annotation { "Feature Type Name" : "Feature", "Feature Type Description" : "" }
export const myFeature = defineFeature(function(context is Context, id is Id, definition is map)
    precondition{}
    {
        {
            var Q0;
            Q0=qCreatedBy(makeId("Top.planeOp"),FACE);
            var sketch = newSketch(context, id + "F0", { "sketchPlane" : qUnion([Q0])});
            skLineSegment(sketch, "E0.bottom", {"start": v(87.5, -50) * mm, "end": v(-62.5, -50) * mm});
            skLineSegment(sketch, "E0.top", {"start": v(87.5, 50) * mm, "end": v(-62.5, 50) * mm});
            skLineSegment(sketch, "E0.left", {"start": v(87.5, -50) * mm, "end": v(87.5, 50) * mm});
            skLineSegment(sketch, "E0.right", {"start": v(-87.5, -20) * mm, "end": v(-87.5, 20) * mm});
            skPoint(sketch, "E0.middle", {"position": v(0, 0) * mm});
            skPoint(sketch, "E1", {"position": v(-87.5, 20) * mm});
            skPoint(sketch, "E2", {"position": v(-62.5, 50) * mm});
            skArc(sketch, "E3", {"start": v(-87.5, 20) * mm, "mid": v(-72.08, 32.56) * mm, "end": v(-62.5, 50) * mm});
            skLineSegment(sketch, "E4", {"start": v(-87.5, 0) * mm, "end": v(87.5, 0) * mm, "construction": true});
            skArc(sketch, "E5.MirrorCS", {"start": v(-87.5, -20) * mm, "mid": v(-72.08, -32.56) * mm, "end": v(-62.5, -50) * mm});
            skPoint(sketch, "E6.orphan", {"position": v(-87.5, 50) * mm});
            skPoint(sketch, "E7.orphan", {"position": v(-87.5, -50) * mm});
            skSolve(sketch);
        }
        {
            var Q0;
            Q0 = qSketchRegion(id + "F0", true);
            extrude(context, id + "F1", {"entities" : qUnion([Q0]), "depth" : 3 * mm, "offsetDistance" : 25 * mm});
        }
        {
            var Q0;
            Q0=makeQuery(id+"F1.opExtrude","CAP_FACE",FACE,{"disambiguationData":[OSD([sQuery(id+"F0.wireOp",EDGE,"E0.bottom"),sQuery(id+"F0.wireOp",EDGE,"E0.top"),sQuery(id+"F0.wireOp",EDGE,"E0.left"),sQuery(id+"F0.wireOp",EDGE,"E0.right"),sQuery(id+"F0.wireOp",EDGE,"E3"),sQuery(id+"F0.wireOp",EDGE,"E5.MirrorCS")])],"isStart":false});
            var sketch = newSketch(context, id + "F2", { "sketchPlane" : qUnion([Q0])});
            skLineSegment(sketch, "E8", {"start": v(-62.5, 50) * mm, "end": v(-62.5, -50) * mm, "construction": true});
            skLineSegment(sketch, "E9", {"start": v(-62.5, 0) * mm, "end": v(-75, 0) * mm, "construction": true});
            skPoint(sketch, "E10", {"position": v(-68.75, 37.02) * mm});
            skLineSegment(sketch, "E11", {"start": v(-68.75, 37.02) * mm, "end": v(-68.75, 0) * mm});
            skLineSegment(sketch, "E12", {"start": v(-78.75, 25.9) * mm, "end": v(-78.75, 0) * mm});
            skArc(sketch, "E13.0", {"start": v(-78.75, 25.9) * mm, "mid": v(-73.35, 31.1) * mm, "end": v(-68.75, 37.02) * mm});
            skPoint(sketch, "E14.orphan", {"position": v(-62.5, 50) * mm});
            skPoint(sketch, "E15.orphan", {"position": v(-87.5, 20) * mm});
            skArc(sketch, "E16.MirrorCS", {"start": v(-78.75, -25.9) * mm, "mid": v(-73.35, -31.1) * mm, "end": v(-68.75, -37.02) * mm});
            skLineSegment(sketch, "E17.MirrorCS", {"start": v(-68.75, -37.02) * mm, "end": v(-68.75, 0) * mm});
            skLineSegment(sketch, "E18.MirrorCS", {"start": v(-78.75, -25.9) * mm, "end": v(-78.75, 0) * mm});
            skSolve(sketch);
        }
        {
            var Q0;
            Q0 = qSketchRegion(id + "F2", true);
            extrude(context, id + "F3", {"entities" : qUnion([Q0]), "operationType" : NewBodyOperationType.ADD, "depth" : 10 * mm, "offsetDistance" : 25 * mm});
        }
        {
            var Q0;
            Q0=makeQuery(id+"F3.opExtrude","CAP_EDGE",EDGE,{"disambiguationData":[OSD([sQuery(id+"F2.wireOp",EDGE,"E11"),sQuery(id+"F2.wireOp",EDGE,"E17.MirrorCS")])],"isStart":false});
            var Q1;
            Q1=makeQuery(id+"F3.opExtrude","CAP_EDGE",EDGE,{"disambiguationData":[OSD([sQuery(id+"F2.wireOp",EDGE,"E12"),sQuery(id+"F2.wireOp",EDGE,"E18.MirrorCS")])],"isStart":false});
            var Q2;
            Q2=makeQuery(id+"F3.opExtrude","CAP_EDGE",EDGE,{"disambiguationData":[OSD([sQuery(id+"F2.wireOp",EDGE,"E11"),sQuery(id+"F2.wireOp",EDGE,"E17.MirrorCS")])],"isStart":true});
            var Q3;
            Q3=makeQuery(id+"F3.opExtrude","CAP_EDGE",EDGE,{"disambiguationData":[OSD([sQuery(id+"F2.wireOp",EDGE,"E12"),sQuery(id+"F2.wireOp",EDGE,"E18.MirrorCS")])],"isStart":true});
            fillet(context, id + "F4", {"entities" : qUnion([Q0, Q1, Q2, Q3]), "radius" : 2 * mm, "tangentPropagation" : true, "allowEdgeOverflow" : false});
        }
        {
            var Q0;
            {var subQ0=sQuery(id+"F0.wireOp",EDGE,"E3");var subQ1=sQuery(id+"F0.wireOp",EDGE,"E0.left");var subQ2=sQuery(id+"F0.wireOp",EDGE,"E0.top");var subQ3=sQuery(id+"F0.wireOp",EDGE,"E0.bottom");var subQ4=sQuery(id+"F0.wireOp",EDGE,"E5.MirrorCS");Q0=makeQuery(id+"F3.boolean.opBoolean","SPLIT",FACE,{"disambiguationData":[TD([makeQuery(id+"F1.opExtrude","SWEPT_FACE",FACE,{"disambiguationData":[OSD([subQ3])]})])],"derivedFrom":makeQuery(id+"F1.opExtrude","CAP_FACE",FACE,{"disambiguationData":[OSD([subQ3,subQ2,subQ1,sQuery(id+"F0.wireOp",EDGE,"E0.right"),subQ0,subQ4])],"isStart":false})});}
            var sketch = newSketch(context, id + "F5", { "sketchPlane" : qUnion([Q0])});
            skText(sketch, "E19", { "text": "ibTECHar", "fontName": "OpenSans-Bold.ttf"});
            skLineSegment(sketch, "E20.bottom", {"start": v(5.5, 45.5) * mm, "end": v(25.5, 45.5) * mm});
            skLineSegment(sketch, "E20.top", {"start": v(5.5, 25.5) * mm, "end": v(25.5, 25.5) * mm});
            skLineSegment(sketch, "E20.left", {"start": v(5.5, 45.5) * mm, "end": v(5.5, 25.5) * mm});
            skLineSegment(sketch, "E20.right", {"start": v(25.5, 45.5) * mm, "end": v(25.5, 25.5) * mm});
            skLineSegment(sketch, "E21", {"start": v(35.5, 26.68) * mm, "end": v(55.5, 26.68) * mm});
            skLineSegment(sketch, "E22", {"start": v(55.5, 26.68) * mm, "end": v(45.5, 44) * mm});
            skLineSegment(sketch, "E23", {"start": v(45.5, 44) * mm, "end": v(35.5, 26.68) * mm});
            skCircle(sketch, "E24", {"center": v(67.25, 36) * mm, "radius": 10 * mm});
            skCircle(sketch, "E25", {"center": v(-59.56, 16.57) * mm, "radius": 5 * mm});
            skCircle(sketch, "E26.1.0.0", {"center": v(-47.06, 16.57) * mm, "radius": 5 * mm});
            skCircle(sketch, "E26.2.0.0", {"center": v(-34.56, 16.57) * mm, "radius": 5 * mm});
            skCircle(sketch, "E26.3.0.0", {"center": v(-22.06, 16.57) * mm, "radius": 5 * mm});
            skCircle(sketch, "E26.4.0.0", {"center": v(-9.56, 16.57) * mm, "radius": 5 * mm});
            skCircle(sketch, "E26.5.0.0", {"center": v(2.94, 16.57) * mm, "radius": 5 * mm});
            skCircle(sketch, "E26.6.0.0", {"center": v(15.44, 16.57) * mm, "radius": 5 * mm});
            skCircle(sketch, "E26.7.0.0", {"center": v(27.94, 16.57) * mm, "radius": 5 * mm});
            skCircle(sketch, "E26.8.0.0", {"center": v(40.44, 16.57) * mm, "radius": 5 * mm});
            skCircle(sketch, "E26.9.0.0", {"center": v(52.94, 16.57) * mm, "radius": 5 * mm});
            skCircle(sketch, "E26.10.0.0", {"center": v(65.44, 16.57) * mm, "radius": 5 * mm});
            skCircle(sketch, "E26.11.0.0", {"center": v(77.94, 16.57) * mm, "radius": 5 * mm});
            skLineSegment(sketch, "E26.direction1", {"start": v(-59.56, 11.57) * mm, "end": v(-47.06, 11.57) * mm, "construction": true});
            skText(sketch, "E27", { "text": "ABCDEFGHIJKLMNOPQ", "fontName": "OpenSans-Bold.ttf"});
            skText(sketch, "E28", { "text": "RSTUV WXYZ", "fontName": "OpenSans-Bold.ttf"});
            skText(sketch, "E29", { "text": "abcdefghijklmnopq", "fontName": "OpenSans-Bold.ttf"});
            skText(sketch, "E30", { "text": "rstuvwxyz", "fontName": "OpenSans-Bold.ttf"});
            skCircle(sketch, "E31", {"center": v(79.71, -37.38) * mm, "radius": 5 * mm});
            skCircle(sketch, "E32", {"center": v(-56.96, -37.38) * mm, "radius": 5 * mm});
            const initialGuessF5  = {"E19": [-0.06595, 0.02657, 1, 0, 0.011], "E27": [-0.06049, -0.00125, 1, 0, 0.009], "E28": [-0.03082, -0.01365, 1, 0, 0.0091], "E29": [-0.0546, -0.02653, 1, 0, 0.00972], "E30": [-0.02796, -0.04027, 1, 0, 0.01051]};
            skSetInitialGuess(sketch, initialGuessF5);
            skSolve(sketch);
        }
        {
            var Q0;
            Q0 = qSketchRegion(id + "F5", true);
            extrude(context, id + "F6", {"entities" : qUnion([Q0]), "operationType" : NewBodyOperationType.REMOVE, "oppositeDirection" : true, "depth" : 25 * mm, "offsetDistance" : 25 * mm});
        }
        {
            var Q0;
            Q0=makeQuery(id+"F1.opExtrude","CAP_EDGE",EDGE,{"disambiguationData":[OSD([sQuery(id+"F0.wireOp",EDGE,"E0.bottom")])],"isStart":false});
            chamfer(context, id + "F7", {"entities" : qUnion([Q0]), "chamferType" : ChamferType.OFFSET_ANGLE, "width" : 3 * mm, "oppositeDirection" : false, "angle" : 60 * degree, "tangentPropagation" : true});
        }
    });